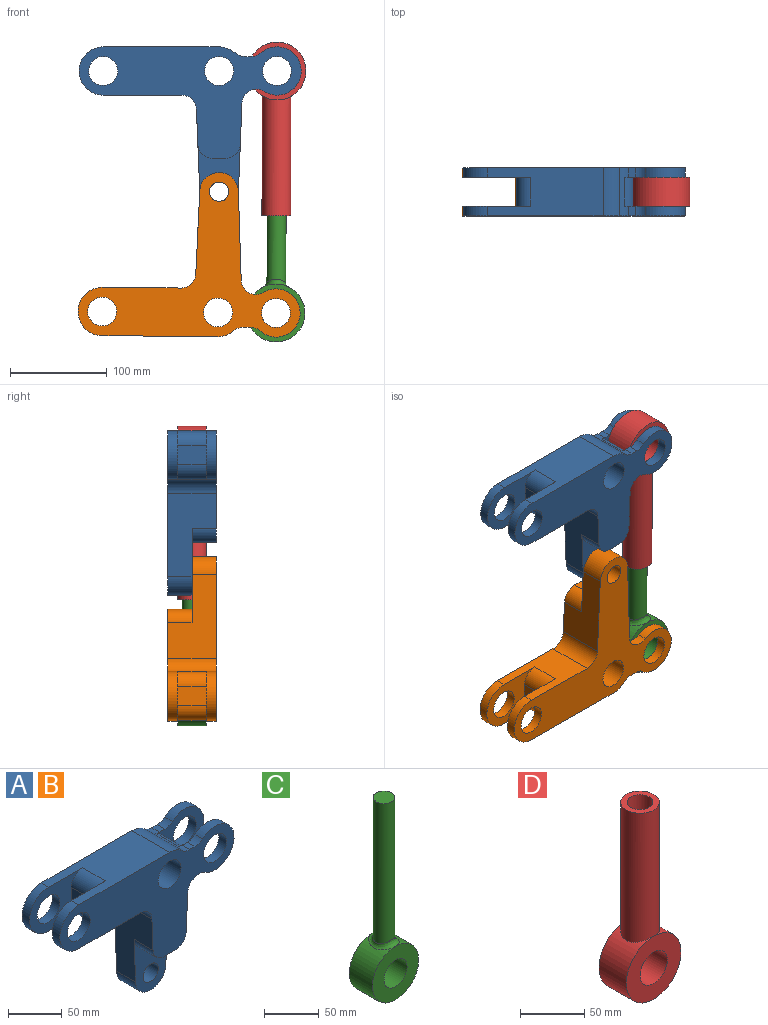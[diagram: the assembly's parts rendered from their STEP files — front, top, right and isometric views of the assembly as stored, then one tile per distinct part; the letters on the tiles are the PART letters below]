
ASSEMBLY  parts=4 mates=4
PART A: 39 faces, bbox 230x50x170 mm
  f0: plane 10x7.09mm, normal (0,0,1), area 70.8mm2, adj f16,f28,f29,f33
  f1: plane 30x14.34mm, normal (1,0,0), area 430.2mm2, adj f22,f28,f37,f38
  f2: plane 30x20mm, normal (-1,0,0), area 600mm2, adj f19,f25,f34,f35
  f3: plane 10x7.09mm, normal (0,0,1), area 70.8mm2, adj f13,f22,f30,f33
  f4: cylinder r=25mm len=50mm, axis (0,-1,0), area 903.4mm2, adj f5,f13,f16,f33
  f5: plane 120x50mm, normal (0,0,1), area 4650mm2, adj f4,f13,f16,f17,f19,f23,f25,f34
  f6: plane 81.57x50mm, normal (0,0,-1), area 2728.6mm2, adj f13,f16,f17,f19,f23,f25,f35,f36
  f7: plane 86.4x50mm, normal (-1,0,-0.04), area 3076.1mm2, adj f8,f13,f14,f16,f31,f36
  f8: cylinder r=20mm len=39.97mm, axis (0,-1,0), area 1530.8mm2, adj f7,f9,f13,f14
  f9: plane 92.56x50mm, normal (1,0,-0.04), area 3384.4mm2, adj f8,f10,f13,f14,f16,f32
  f10: cylinder r=15mm len=50mm, axis (0,-1,0), area 958.1mm2, adj f9,f13,f16,f20,f22,f26,f28,f37
  f11: cylinder r=15mm len=50mm, axis (0,-1,0), area 4712.4mm2, adj f13,f16
  f12: cylinder r=10mm len=25mm, axis (0,-1,0), area 1570.8mm2, adj f13,f14
  f13: plane 230x170mm, normal (0,1,0), area 13187.8mm2, adj f3,f4,f5,f6,f7,f8,f9,f10
  f14: plane 69.05x43.96mm, normal (0,-1,0), area 1837.2mm2, adj f7,f8,f9,f12,f15,f31,f32
  f15: plane 25x13.98mm, normal (0,0,-1), area 349.5mm2, adj f14,f16,f31,f32
  f16: plane 230x115.35mm, normal (0,-1,0), area 11350.6mm2, adj f0,f4,f5,f6,f7,f9,f10,f11
  f17: cylinder r=25mm len=50mm, axis (0,1,0), area 785.4mm2, adj f5,f6,f13,f19
  f18: cylinder r=15mm len=30mm, axis (0,1,0), area 942.5mm2, adj f13,f19
  f19: plane 70x50mm, normal (0,-1,0), area 1871.5mm2, adj f2,f5,f6,f17,f18,f34,f35
  f20: cylinder r=25mm len=50mm, axis (0,1,0), area 1106.7mm2, adj f10,f13,f22,f30
  f21: cylinder r=15mm len=30mm, axis (0,1,0), area 942.5mm2, adj f13,f22
  f22: plane 63.17x50mm, normal (0,-1,0), area 1474.2mm2, adj f1,f3,f10,f20,f21,f30,f33,f37
  f23: cylinder r=25mm len=50mm, axis (0,-1,0), area 785.4mm2, adj f5,f6,f16,f25
  f24: cylinder r=15mm len=30mm, axis (0,-1,0), area 942.5mm2, adj f16,f25
  f25: plane 70x50mm, normal (0,1,0), area 1871.5mm2, adj f2,f5,f6,f23,f24,f34,f35
  f26: cylinder r=25mm len=50mm, axis (0,-1,0), area 1106.7mm2, adj f10,f16,f28,f29
  f27: cylinder r=15mm len=30mm, axis (0,-1,0), area 942.5mm2, adj f16,f28
  f28: plane 63.17x50mm, normal (0,1,0), area 1474.2mm2, adj f0,f1,f10,f26,f27,f29,f33,f37
  f29: cylinder r=15mm len=10mm, axis (0,-1,0), area 108.4mm2, adj f0,f16,f26,f28
  f30: cylinder r=15mm len=10mm, axis (0,1,0), area 108.4mm2, adj f3,f13,f20,f22
  f31: cylinder r=15mm len=25mm, axis (0,1,0), area 574.1mm2, adj f7,f14,f15,f16
  f32: cylinder r=15mm len=25mm, axis (0,-1,0), area 574.1mm2, adj f9,f14,f15,f16
  f33: cylinder r=15mm len=50mm, axis (0,-1,0), area 401mm2, adj f0,f3,f4,f13,f16,f22,f28,f38
  f34: cylinder r=15mm len=30mm, axis (0,1,0), area 706.9mm2, adj f2,f5,f19,f25
  f35: cylinder r=15mm len=30mm, axis (0,-1,0), area 706.9mm2, adj f2,f6,f19,f25
  f36: cylinder r=15mm len=50mm, axis (0,-1,0), area 1148.1mm2, adj f6,f7,f13,f16
  f37: cylinder r=15mm len=30mm, axis (0,-1,0), area 348.1mm2, adj f1,f10,f22,f28
  f38: cylinder r=15mm len=30mm, axis (0,-1,0), area 565.8mm2, adj f1,f22,f28,f33
PART B: same geometry as A
PART C: 7 faces, bbox 60x30x220 mm
  f0: cylinder r=15mm len=30mm, axis (0,1,0), area 2827.4mm2, adj f2,f3
  f1: cylinder r=30mm len=60mm, axis (0,1,0), area 5034.5mm2, adj f2,f3,f6
  f2: plane 60x60mm, normal (0,-1,0), area 2120.6mm2, adj f0,f1
  f3: plane 60x60mm, normal (0,1,0), area 2120.6mm2, adj f0,f1
  f4: plane 20x20mm, normal (0,0,1), area 314.2mm2, adj f5
  f5: cylinder r=10mm len=158.38mm, axis (0,0,1), area 9843.7mm2, adj f4,f6
  f6: bspline ~30.03x25.73mm, area 487.9mm2, adj f1,f5
PART D: 8 faces, bbox 60x30x180 mm
  f0: cylinder r=15mm len=30mm, axis (0,1,0), area 2827.4mm2, adj f2,f3
  f1: cylinder r=30mm len=60mm, axis (0,1,0), area 4923.9mm2, adj f2,f3,f5
  f2: plane 60x60mm, normal (0,-1,0), area 2120.6mm2, adj f0,f1
  f3: plane 60x60mm, normal (0,1,0), area 2120.6mm2, adj f0,f1
  f4: plane 30x30mm, normal (0,0,1), area 392.7mm2, adj f5,f6
  f5: cylinder r=15mm len=124.02mm, axis (0,0,1), area 11495.8mm2, adj f1,f4
  f6: cylinder r=10mm len=110mm, axis (0,0,1), area 6911.5mm2, adj f4,f7
  f7: plane 20x20mm, normal (0,0,1), area 314.2mm2, adj f6
PLACE A t=(-56.94,12.19,49.65)mm fixed
PLACE B rot(axis=(-1,0,0),180deg) t=(-57.99,12.19,-199.33)mm
PLACE C rot(axis=(0,1,0),0.2deg) t=(122,12.19,-200.85)mm
PLACE D rot(axis=(0,-1,0),179.8deg) t=(123.06,12.19,49.65)mm
MATE revolute C.f0 <-> B.f21  axis (0,-1,0) through (122,-2.81,-200.85)mm
MATE slider C.f5 <-> D.f5  axis (0,0,1) through (122.47,12.19,-90.53)mm
MATE revolute B.f8 <-> A.f8  axis (0,1,0) through (63.06,12.19,-75.35)mm
MATE revolute D.f1 <-> A.f21  axis (0,-1,0) through (123.06,-2.81,49.65)mm
